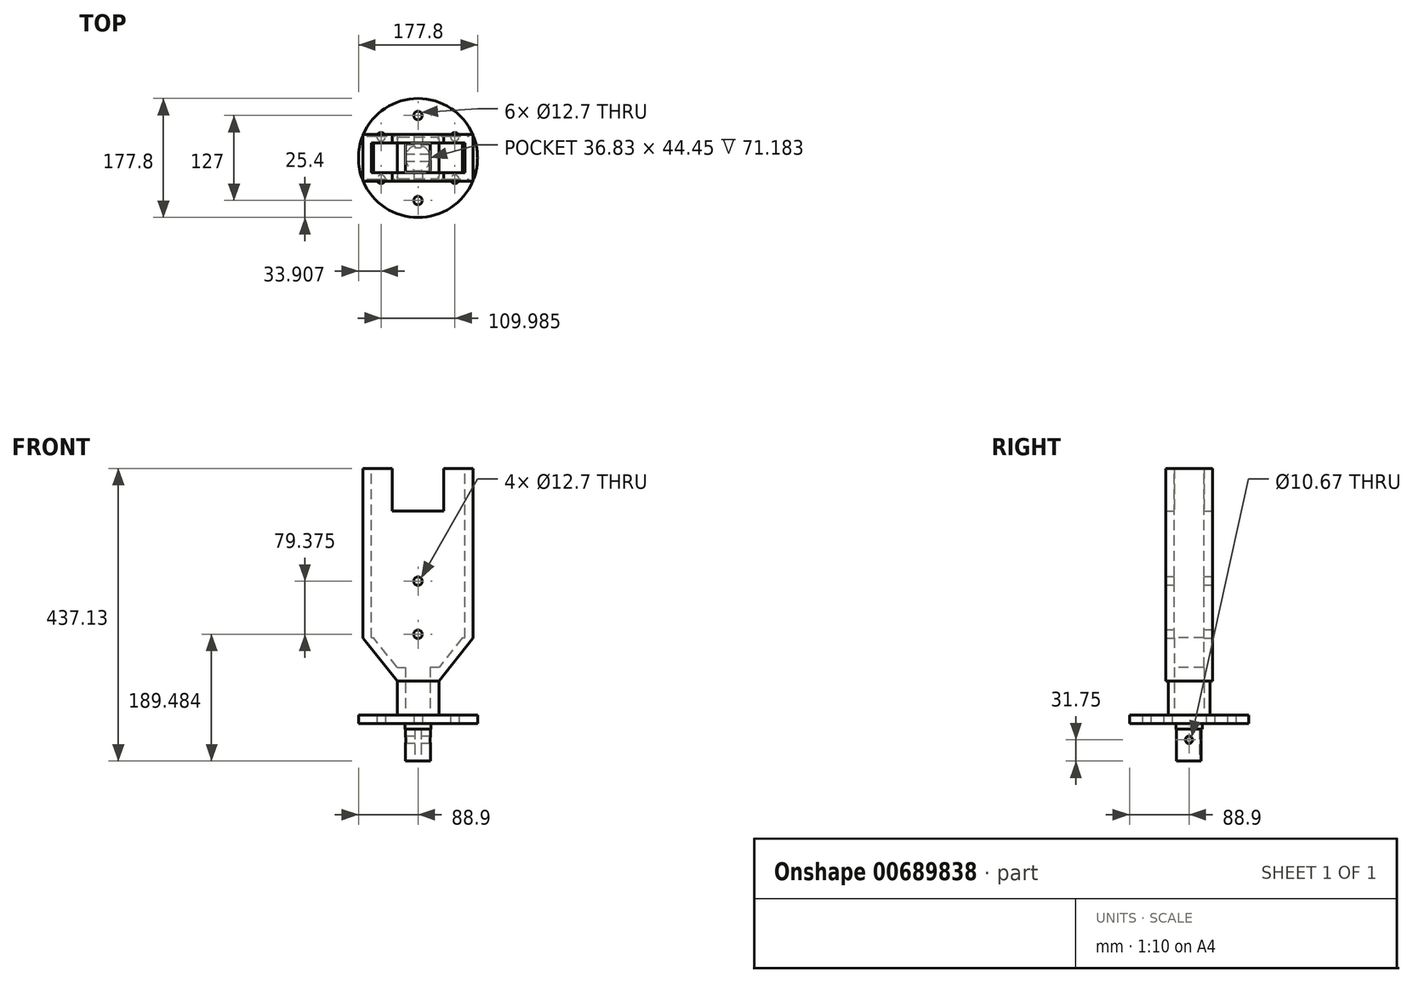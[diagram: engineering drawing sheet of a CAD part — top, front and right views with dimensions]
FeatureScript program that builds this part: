
annotation { "Feature Type Name" : "Feature", "Feature Type Description" : "" }
export const myFeature = defineFeature(function(context is Context, id is Id, definition is map)
    precondition{}
    {
        {
            var Q0;
            Q0=qCreatedBy(makeId("Top.planeOp"),FACE);
            var sketch = newSketch(context, id + "F0", { "sketchPlane" : qUnion([Q0])});
            skArc(sketch, "E0", {"start": v(-4.76, 18.18) * mm, "mid": v(0, -18.8) * mm, "end": v(4.76, 18.18) * mm});
            skLineSegment(sketch, "E1.top", {"start": v(-4.76, 15.42) * mm, "end": v(4.76, 15.42) * mm});
            skLineSegment(sketch, "E1.left", {"start": v(-4.76, 18.18) * mm, "end": v(-4.76, 15.42) * mm});
            skLineSegment(sketch, "E1.right", {"start": v(4.76, 18.18) * mm, "end": v(4.76, 15.42) * mm});
            skLineSegment(sketch, "E2", {"start": v(0, 0) * mm, "end": v(0, 15.42) * mm, "construction": true});
            skSolve(sketch);
        }
        {
            var Q0;
            Q0 = qSketchRegion(id + "F0", true);
            extrude(context, id + "F1", {"entities" : qUnion([Q0]), "depth" : 47.75 * mm, "offsetDistance" : 25.4 * mm});
        }
        {
            var Q0;
            Q0=makeQuery(id+"F1.opExtrude","CAP_FACE",FACE,{"disambiguationData":[OSD([sQuery(id+"F0.wireOp",EDGE,"E0"),sQuery(id+"F0.wireOp",EDGE,"E1.top"),sQuery(id+"F0.wireOp",EDGE,"E1.left"),sQuery(id+"F0.wireOp",EDGE,"E1.right")])],"isStart":false});
            var sketch = newSketch(context, id + "F2", { "sketchPlane" : qUnion([Q0])});
            skLineSegment(sketch, "E3.bottom", {"start": v(-19.68, 19.69) * mm, "end": v(19.69, 19.69) * mm});
            skLineSegment(sketch, "E3.top", {"start": v(-19.69, -19.69) * mm, "end": v(19.68, -19.69) * mm});
            skLineSegment(sketch, "E3.left", {"start": v(-19.68, 19.69) * mm, "end": v(-19.69, -19.69) * mm});
            skLineSegment(sketch, "E3.right", {"start": v(19.69, 19.69) * mm, "end": v(19.69, -19.69) * mm});
            skPoint(sketch, "E3.middle", {"position": v(0, 0) * mm});
            skSolve(sketch);
        }
        {
            var Q0;
            Q0 = qSketchRegion(id + "F2", true);
            extrude(context, id + "F3", {"entities" : qUnion([Q0]), "operationType" : NewBodyOperationType.ADD, "depth" : 8.38 * mm, "offsetDistance" : 25.4 * mm});
        }
        {
            var Q0;
            Q0=makeQuery(id+"F3.opExtrude","CAP_FACE",FACE,{"disambiguationData":[OSD([sQuery(id+"F2.wireOp",EDGE,"E3.bottom"),sQuery(id+"F2.wireOp",EDGE,"E3.top"),sQuery(id+"F2.wireOp",EDGE,"E3.left"),sQuery(id+"F2.wireOp",EDGE,"E3.right")])],"isStart":false});
            var sketch = newSketch(context, id + "F4", { "sketchPlane" : qUnion([Q0])});
            skCircle(sketch, "E4", {"center": v(0, 0) * mm, "radius": 88.9 * mm});
            skCircle(sketch, "E5", {"center": v(0, 63.5) * mm, "radius": 6.35 * mm});
            skCircle(sketch, "E6.1.0", {"center": v(-55, 31.75) * mm, "radius": 6.35 * mm});
            skCircle(sketch, "E6.2.0", {"center": v(-55, -31.75) * mm, "radius": 6.35 * mm});
            skCircle(sketch, "E6.3.0", {"center": v(0, -63.5) * mm, "radius": 6.35 * mm});
            skCircle(sketch, "E6.4.0", {"center": v(55, -31.75) * mm, "radius": 6.35 * mm});
            skCircle(sketch, "E6.5.0", {"center": v(55, 31.75) * mm, "radius": 6.35 * mm});
            skSolve(sketch);
        }
        {
            var Q0;
            Q0 = qSketchRegion(id + "F4", true);
            extrude(context, id + "F5", {"entities" : qUnion([Q0]), "operationType" : NewBodyOperationType.ADD, "depth" : 12.7 * mm, "offsetDistance" : 25.4 * mm});
        }
        {
            var Q0;
            Q0=makeQuery(id+"F5.opExtrude","CAP_FACE",FACE,{"disambiguationData":[OSD([sQuery(id+"F4.wireOp",EDGE,"E4"),sQuery(id+"F4.wireOp",EDGE,"E5"),sQuery(id+"F4.wireOp",EDGE,"E6.1.0"),sQuery(id+"F4.wireOp",EDGE,"E6.2.0"),sQuery(id+"F4.wireOp",EDGE,"E6.3.0"),sQuery(id+"F4.wireOp",EDGE,"E6.4.0"),sQuery(id+"F4.wireOp",EDGE,"E6.5.0")])],"isStart":false});
            var sketch = newSketch(context, id + "F6", { "sketchPlane" : qUnion([Q0])});
            skLineSegment(sketch, "E7.bottom", {"start": v(-27.3, 31.12) * mm, "end": v(27.3, 31.12) * mm});
            skLineSegment(sketch, "E7.top", {"start": v(-27.3, -31.12) * mm, "end": v(27.3, -31.12) * mm});
            skLineSegment(sketch, "E7.left", {"start": v(-31.12, 27.3) * mm, "end": v(-31.12, -27.3) * mm});
            skLineSegment(sketch, "E7.right", {"start": v(31.12, 27.3) * mm, "end": v(31.12, -27.3) * mm});
            skPoint(sketch, "E7.middle", {"position": v(0, 0) * mm});
            skPoint(sketch, "E8.visualSharp", {"position": v(-31.12, 31.12) * mm});
            skArc(sketch, "E8.filletArc", {"start": v(-27.3, 31.12) * mm, "mid": v(-30, 30) * mm, "end": v(-31.12, 27.3) * mm});
            skPoint(sketch, "E9.visualSharp", {"position": v(31.12, 31.12) * mm});
            skArc(sketch, "E9.filletArc", {"start": v(31.12, 27.3) * mm, "mid": v(30, 30) * mm, "end": v(27.3, 31.12) * mm});
            skPoint(sketch, "E10.visualSharp", {"position": v(31.12, -31.11) * mm});
            skArc(sketch, "E10.filletArc", {"start": v(27.3, -31.12) * mm, "mid": v(30, -30) * mm, "end": v(31.12, -27.3) * mm});
            skPoint(sketch, "E11.visualSharp", {"position": v(-31.12, -31.12) * mm});
            skArc(sketch, "E11.filletArc", {"start": v(-31.12, -27.3) * mm, "mid": v(-30, -30) * mm, "end": v(-27.3, -31.12) * mm});
            skSolve(sketch);
        }
        {
            var Q0;
            Q0 = qSketchRegion(id + "F6", true);
            extrude(context, id + "F7", {"entities" : qUnion([Q0]), "operationType" : NewBodyOperationType.ADD, "depth" : 50.8 * mm, "offsetDistance" : 25.4 * mm});
        }
        {
            var Q0;
            Q0=qCreatedBy(makeId("Right.planeOp"),FACE);
            var sketch = newSketch(context, id + "F8", { "sketchPlane" : qUnion([Q0])});
            skCircle(sketch, "E12", {"center": v(0, 31.75) * mm, "radius": 5.33 * mm});
            skSolve(sketch);
        }
        {
            var Q0;
            Q0 = qSketchRegion(id + "F8", true);
            extrude(context, id + "F9", {"entities" : qUnion([Q0]), "operationType" : NewBodyOperationType.REMOVE, "endBound" : BoundingType.THROUGH_ALL, "depth" : 25.4 * mm, "offsetDistance" : 25.4 * mm, "hasSecondDirection" : true, "secondDirectionOppositeDirection" : true, "secondDirectionDepth" : 127 * mm});
        }
        {
            var Q0;
            Q0=makeQuery(id+"F7.opExtrude","CAP_FACE",FACE,{"disambiguationData":[OSD([sQuery(id+"F6.wireOp",EDGE,"E7.bottom"),sQuery(id+"F6.wireOp",EDGE,"E7.top"),sQuery(id+"F6.wireOp",EDGE,"E7.left"),sQuery(id+"F6.wireOp",EDGE,"E7.right"),sQuery(id+"F6.wireOp",EDGE,"E8.filletArc"),sQuery(id+"F6.wireOp",EDGE,"E9.filletArc"),sQuery(id+"F6.wireOp",EDGE,"E10.filletArc"),sQuery(id+"F6.wireOp",EDGE,"E11.filletArc")])],"isStart":false});
            var sketch = newSketch(context, id + "F10", { "sketchPlane" : qUnion([Q0])});
            skArc(sketch, "E13.0.0", {"start": v(-31.12, -27.3) * mm, "mid": v(-30, -30) * mm, "end": v(-27.3, -31.12) * mm, "construction": true});
            skLineSegment(sketch, "E13.0.1", {"start": v(-27.3, -31.12) * mm, "end": v(27.3, -31.12) * mm, "construction": true});
            skArc(sketch, "E13.0.2", {"start": v(27.3, -31.12) * mm, "mid": v(30, -30) * mm, "end": v(31.12, -27.3) * mm, "construction": true});
            skLineSegment(sketch, "E13.0.3", {"start": v(31.12, -27.3) * mm, "end": v(31.12, 27.3) * mm, "construction": true});
            skArc(sketch, "E13.0.4", {"start": v(31.12, 27.3) * mm, "mid": v(30, 30) * mm, "end": v(27.3, 31.12) * mm, "construction": true});
            skLineSegment(sketch, "E13.0.5", {"start": v(27.3, 31.12) * mm, "end": v(-27.3, 31.12) * mm, "construction": true});
            skArc(sketch, "E13.0.6", {"start": v(-27.3, 31.12) * mm, "mid": v(-30, 30) * mm, "end": v(-31.12, 27.3) * mm, "construction": true});
            skLineSegment(sketch, "E13.0.7", {"start": v(-31.12, 27.3) * mm, "end": v(-31.12, -27.3) * mm, "construction": true});
            skLineSegment(sketch, "E14.0", {"start": v(18.42, 18.42) * mm, "end": v(-18.42, 18.42) * mm});
            skLineSegment(sketch, "E14.1", {"start": v(18.42, -18.42) * mm, "end": v(18.42, 18.42) * mm});
            skLineSegment(sketch, "E14.2", {"start": v(-18.42, -18.42) * mm, "end": v(18.42, -18.42) * mm});
            skLineSegment(sketch, "E14.3", {"start": v(-18.42, 18.42) * mm, "end": v(-18.42, -18.42) * mm});
            skSolve(sketch);
        }
        {
            var Q0;
            Q0 = qSketchRegion(id + "F10", true);
            var Q1;
            Q1=makeQuery(id+"F5.opExtrude","CAP_FACE",FACE,{"disambiguationData":[OSD([sQuery(id+"F4.wireOp",EDGE,"E4"),sQuery(id+"F4.wireOp",EDGE,"E5"),sQuery(id+"F4.wireOp",EDGE,"E6.1.0"),sQuery(id+"F4.wireOp",EDGE,"E6.2.0"),sQuery(id+"F4.wireOp",EDGE,"E6.3.0"),sQuery(id+"F4.wireOp",EDGE,"E6.4.0"),sQuery(id+"F4.wireOp",EDGE,"E6.5.0")])],"isStart":false});
            extrude(context, id + "F11", {"entities" : qUnion([Q0]), "operationType" : NewBodyOperationType.REMOVE, "endBound" : BoundingType.UP_TO_SURFACE, "oppositeDirection" : true, "depth" : 25.4 * mm, "endBoundEntityFace" : qUnion([Q1]), "offsetDistance" : 25.4 * mm});
        }
        {
            var Q0;
            Q0=qCreatedBy(makeId("Front.planeOp"),FACE);
            var sketch = newSketch(context, id + "F12", { "sketchPlane" : qUnion([Q0])});
            skLineSegment(sketch, "E15.0", {"start": v(31.12, 119.63) * mm, "end": v(31.12, 68.83) * mm, "construction": true});
            skLineSegment(sketch, "E16", {"start": v(31.11, 119.63) * mm, "end": v(82.55, 184.2) * mm});
            skLineSegment(sketch, "E17", {"start": v(82.55, 184.2) * mm, "end": v(82.55, 437.13) * mm});
            skLineSegment(sketch, "E18", {"start": v(82.55, 437.13) * mm, "end": v(38.35, 437.13) * mm});
            skLineSegment(sketch, "E19", {"start": v(38.35, 437.13) * mm, "end": v(38.35, 373.63) * mm});
            skLineSegment(sketch, "E20", {"start": v(38.35, 373.63) * mm, "end": v(0, 373.63) * mm});
            skLineSegment(sketch, "E21", {"start": v(0, 373.63) * mm, "end": v(0, 119.63) * mm, "construction": true});
            skLineSegment(sketch, "E22", {"start": v(0, 119.63) * mm, "end": v(31.12, 119.63) * mm});
            skLineSegment(sketch, "E23.MirrorCS", {"start": v(-38.35, 373.63) * mm, "end": v(0, 373.63) * mm});
            skLineSegment(sketch, "E24.MirrorCS", {"start": v(-38.35, 437.13) * mm, "end": v(-38.35, 373.63) * mm});
            skLineSegment(sketch, "E25.MirrorCS", {"start": v(-82.55, 437.13) * mm, "end": v(-38.35, 437.13) * mm});
            skLineSegment(sketch, "E26.MirrorCS", {"start": v(-82.55, 184.2) * mm, "end": v(-82.55, 437.13) * mm});
            skLineSegment(sketch, "E27.MirrorCS", {"start": v(-31.11, 119.63) * mm, "end": v(-82.55, 184.2) * mm});
            skLineSegment(sketch, "E28.MirrorCS", {"start": v(0, 119.63) * mm, "end": v(-31.12, 119.63) * mm});
            skSolve(sketch);
        }
        {
            var Q0;
            Q0 = qSketchRegion(id + "F12", true);
            extrude(context, id + "F13", {"entities" : qUnion([Q0]), "operationType" : NewBodyOperationType.ADD, "endBound" : BoundingType.SYMMETRIC, "depth" : 69.85 * mm, "offsetDistance" : 25.4 * mm});
        }
        {
            var Q0;
            Q0=makeQuery(id+"F13.opExtrude","SWEPT_FACE",FACE,{"disambiguationData":[OSD([sQuery(id+"F12.wireOp",EDGE,"E18")])]});
            var sketch = newSketch(context, id + "F14", { "sketchPlane" : qUnion([Q0])});
            skLineSegment(sketch, "E29.bottom", {"start": v(-69.85, 22.23) * mm, "end": v(69.85, 22.23) * mm});
            skLineSegment(sketch, "E29.top", {"start": v(-69.85, -22.23) * mm, "end": v(69.85, -22.23) * mm});
            skLineSegment(sketch, "E29.left", {"start": v(-69.85, 22.23) * mm, "end": v(-69.85, -22.23) * mm});
            skLineSegment(sketch, "E29.right", {"start": v(69.85, 22.23) * mm, "end": v(69.85, -22.23) * mm});
            skPoint(sketch, "E29.middle", {"position": v(0, 0) * mm});
            skSolve(sketch);
        }
        {
            var Q0;
            Q0 = qSketchRegion(id + "F14", true);
            var Q1;
            Q1=makeQuery(id+"F13.opExtrude","CAP_VERTEX",VERTEX,{"disambiguationData":[OSD([sQuery(id+"F12.wireOp",EDGE,"E26.MirrorCS"),sQuery(id+"F12.wireOp",EDGE,"E27.MirrorCS")])],"isStart":true});
            extrude(context, id + "F15", {"entities" : qUnion([Q0]), "operationType" : NewBodyOperationType.REMOVE, "endBound" : BoundingType.UP_TO_VERTEX, "oppositeDirection" : true, "depth" : 25.4 * mm, "endBoundEntityVertex" : qUnion([Q1]), "offsetDistance" : 25.4 * mm});
        }
        {
            var Q0;
            Q0=qCreatedBy(makeId("Front.planeOp"),FACE);
            var sketch = newSketch(context, id + "F16", { "sketchPlane" : qUnion([Q0])});
            skLineSegment(sketch, "E30", {"start": v(66.31, 184.2) * mm, "end": v(-66.31, 184.2) * mm});
            skLineSegment(sketch, "E31", {"start": v(66.31, 184.2) * mm, "end": v(31.12, 140.02) * mm});
            skLineSegment(sketch, "E32", {"start": v(-31.12, 140.02) * mm, "end": v(31.12, 140.02) * mm, "construction": true});
            skLineSegment(sketch, "E33", {"start": v(-31.12, 140.02) * mm, "end": v(-66.31, 184.2) * mm});
            skLineSegment(sketch, "E34.top", {"start": v(18.42, 68.83) * mm, "end": v(-18.41, 68.83) * mm});
            skLineSegment(sketch, "E34.left", {"start": v(-18.41, 140.02) * mm, "end": v(-18.41, 68.83) * mm});
            skLineSegment(sketch, "E34.right", {"start": v(18.42, 140.02) * mm, "end": v(18.42, 68.83) * mm});
            skLineSegment(sketch, "E35", {"start": v(-31.12, 140.02) * mm, "end": v(-18.41, 140.02) * mm});
            skLineSegment(sketch, "E36", {"start": v(31.12, 140.02) * mm, "end": v(18.42, 140.02) * mm});
            skSolve(sketch);
        }
        {
            var Q0;
            Q0 = qSketchRegion(id + "F16", true);
            extrude(context, id + "F17", {"entities" : qUnion([Q0]), "operationType" : NewBodyOperationType.REMOVE, "endBound" : BoundingType.SYMMETRIC, "oppositeDirection" : true, "depth" : 44.45 * mm, "offsetDistance" : 25.4 * mm});
        }
        {
            var Q0;
            Q0=makeQuery(id+"F13.opExtrude","SWEPT_EDGE",EDGE,{"disambiguationData":[OSD([sQuery(id+"F12.wireOp",EDGE,"E16"),sQuery(id+"F12.wireOp",EDGE,"E17")])]});
            var Q1;
            Q1=makeQuery(id+"F13.opExtrude","SWEPT_EDGE",EDGE,{"disambiguationData":[OSD([sQuery(id+"F12.wireOp",EDGE,"E26.MirrorCS"),sQuery(id+"F12.wireOp",EDGE,"E27.MirrorCS")])]});
            fillet(context, id + "F18", {"entities" : qUnion([Q0, Q1]), "tangentPropagation" : true, "radius" : 5.08 * mm, "defaultsChanged" : false, "vertexSettings" : [], "allowEdgeOverflow" : false});
        }
        {
            var Q0;
            Q0=makeQuery(id+"F13.opExtrude","CAP_FACE",FACE,{"disambiguationData":[OSD([sQuery(id+"F12.wireOp",EDGE,"E16"),sQuery(id+"F12.wireOp",EDGE,"E17"),sQuery(id+"F12.wireOp",EDGE,"E18"),sQuery(id+"F12.wireOp",EDGE,"E19"),sQuery(id+"F12.wireOp",EDGE,"E20"),sQuery(id+"F12.wireOp",EDGE,"E22"),sQuery(id+"F12.wireOp",EDGE,"E23.MirrorCS"),sQuery(id+"F12.wireOp",EDGE,"E24.MirrorCS"),sQuery(id+"F12.wireOp",EDGE,"E25.MirrorCS"),sQuery(id+"F12.wireOp",EDGE,"E26.MirrorCS"),sQuery(id+"F12.wireOp",EDGE,"E27.MirrorCS"),sQuery(id+"F12.wireOp",EDGE,"E28.MirrorCS")])],"isStart":false});
            var sketch = newSketch(context, id + "F19", { "sketchPlane" : qUnion([Q0])});
            skCircle(sketch, "E37", {"center": v(0, 189.48) * mm, "radius": 6.35 * mm});
            skCircle(sketch, "E38", {"center": v(0, 268.86) * mm, "radius": 6.35 * mm});
            skSolve(sketch);
        }
        {
            var Q0;
            Q0 = qSketchRegion(id + "F19", true);
            extrude(context, id + "F20", {"entities" : qUnion([Q0]), "operationType" : NewBodyOperationType.REMOVE, "endBound" : BoundingType.THROUGH_ALL, "oppositeDirection" : true, "depth" : 25.4 * mm, "offsetDistance" : 25.4 * mm});
        }
    });
